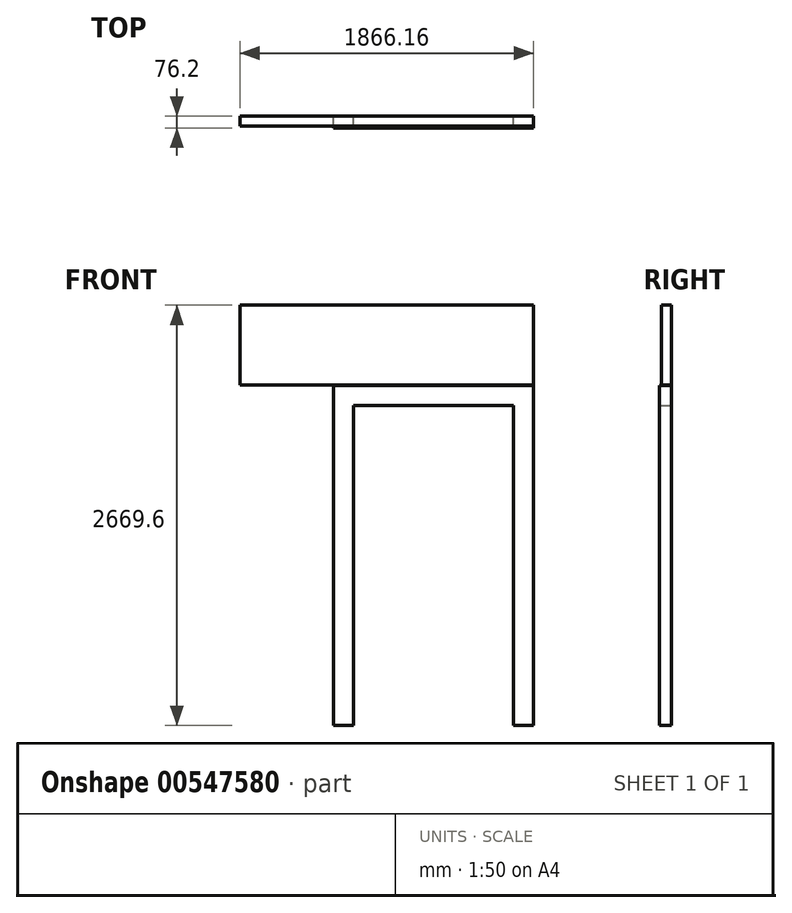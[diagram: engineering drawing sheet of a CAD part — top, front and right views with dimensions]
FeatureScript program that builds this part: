
annotation { "Feature Type Name" : "Feature", "Feature Type Description" : "" }
export const myFeature = defineFeature(function(context is Context, id is Id, definition is map)
    precondition{}
    {
        {
            var Q0;
            Q0=qCreatedBy(makeId("Front.planeOp"),FACE);
            var sketch = newSketch(context, id + "F0", { "sketchPlane" : qUnion([Q0])});
            skLineSegment(sketch, "E0.bottom", {"start": v(-635, 1079.5) * mm, "end": v(635, 1079.5) * mm});
            skLineSegment(sketch, "E0.left", {"start": v(-635, 1079.5) * mm, "end": v(-635, -1079.5) * mm});
            skLineSegment(sketch, "E0.right", {"start": v(635, 1079.5) * mm, "end": v(635, -1079.5) * mm});
            skPoint(sketch, "E0.middle", {"position": v(0, 0) * mm});
            skLineSegment(sketch, "E1", {"start": v(-508, -1079.5) * mm, "end": v(-508, 952.5) * mm});
            skLineSegment(sketch, "E2", {"start": v(-508, 952.5) * mm, "end": v(508, 952.5) * mm});
            skLineSegment(sketch, "E3", {"start": v(508, 952.5) * mm, "end": v(508, -1079.5) * mm});
            skLineSegment(sketch, "E4", {"start": v(508, -1079.5) * mm, "end": v(635, -1079.5) * mm});
            skLineSegment(sketch, "E5", {"start": v(-635, -1079.5) * mm, "end": v(-508, -1079.5) * mm});
            skSolve(sketch);
        }
        {
            var Q0;
            Q0=makeQuery(id+"F0.imprint","IMPRINT",FACE,{"disambiguationData":[TD([[makeQuery(id+"F0.imprint","IMPRINT",EDGE,{"derivedFrom":sQuery(id+"F0.wireOp",EDGE,"E0.bottom")}),-1.0]])]});
            extrude(context, id + "F1", {"entities" : qUnion([Q0]), "depth" : 76.2 * mm, "offsetDistance" : 25.4 * mm});
        }
        {
            var Q0;
            Q0=qCreatedBy(makeId("Front.planeOp"),FACE);
            var sketch = newSketch(context, id + "F2", { "sketchPlane" : qUnion([Q0])});
            skLineSegment(sketch, "E6.bottom", {"start": v(633.45, 1082.1) * mm, "end": v(-1231.16, 1082.1) * mm});
            skLineSegment(sketch, "E6.top", {"start": v(633.45, 1590.1) * mm, "end": v(-1231.16, 1590.1) * mm});
            skLineSegment(sketch, "E6.left", {"start": v(633.45, 1082.1) * mm, "end": v(633.45, 1590.1) * mm});
            skLineSegment(sketch, "E6.right", {"start": v(-1231.16, 1082.1) * mm, "end": v(-1231.16, 1590.1) * mm});
            skLineSegment(sketch, "E7.bottom", {"start": v(-1231.16, 1082.1) * mm, "end": v(-638.38, 1082.1) * mm});
            skLineSegment(sketch, "E7.top", {"start": v(-1231.16, -1076.9) * mm, "end": v(-638.38, -1076.9) * mm});
            skLineSegment(sketch, "E7.left", {"start": v(-1231.16, 1082.1) * mm, "end": v(-1231.16, -1076.9) * mm});
            skLineSegment(sketch, "E7.right", {"start": v(-638.38, 1082.1) * mm, "end": v(-638.38, -1076.9) * mm});
            skSolve(sketch);
        }
        {
            var Q0;
            Q0=makeQuery(id+"F2.imprint","IMPRINT",FACE,{"disambiguationData":[TD([[makeQuery(id+"F2.imprint","IMPRINT",EDGE,{"derivedFrom":sQuery(id+"F2.wireOp",EDGE,"E6.bottom")}),-1.0]])]});
            var Q1;
            Q1=makeQuery(id+"F2.imprint","IMPRINT",FACE,{"disambiguationData":[TD([[makeQuery(id+"F2.imprint","IMPRINT",EDGE,{"derivedFrom":sQuery(id+"F2.wireOp",EDGE,"E7.bottom")}),-1.0]])]});
            extrude(context, id + "F3", {"entities" : qUnion([Q0, Q1]), "depth" : 63.5 * mm, "offsetDistance" : 25.4 * mm});
        }
    });
